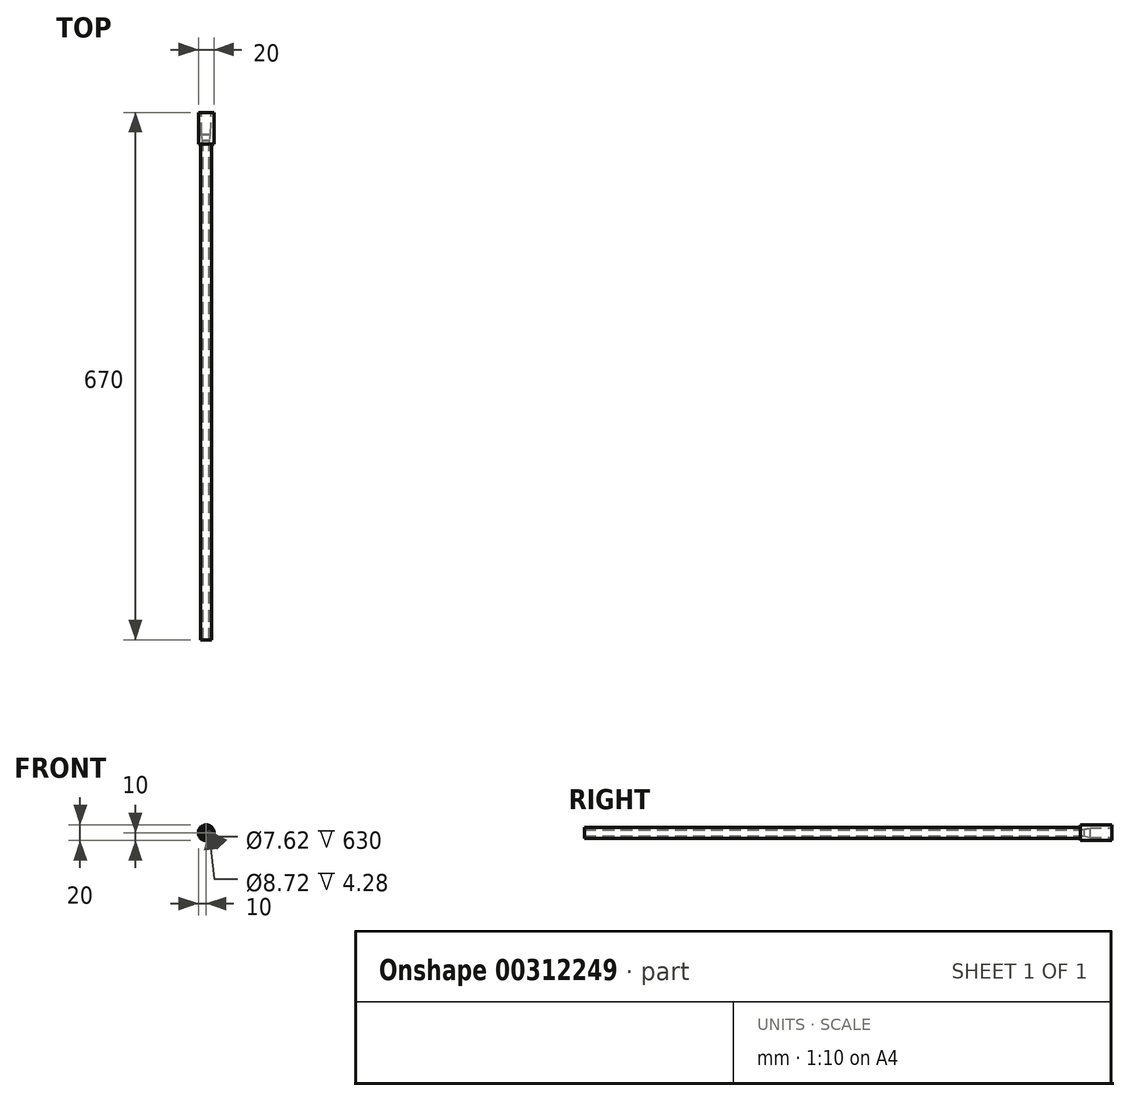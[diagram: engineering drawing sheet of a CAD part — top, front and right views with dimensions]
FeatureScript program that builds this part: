
annotation { "Feature Type Name" : "Feature", "Feature Type Description" : "" }
export const myFeature = defineFeature(function(context is Context, id is Id, definition is map)
    precondition{}
    {
        {
            var Q0;
            Q0=qCreatedBy(makeId("Front.planeOp"),FACE);
            var sketch = newSketch(context, id + "F0", { "sketchPlane" : qUnion([Q0])});
            skCircle(sketch, "E0", {"center": v(0, 0) * mm, "radius": 7 * mm});
            skCircle(sketch, "E1", {"center": v(0, 0) * mm, "radius": 3.81 * mm});
            skSolve(sketch);
        }
        {
            var Q0;
            Q0=makeQuery(id+"F0.imprint","IMPRINT",FACE,{"disambiguationData":[TD([[makeQuery(id+"F0.imprint","IMPRINT",EDGE,{"derivedFrom":sQuery(id+"F0.wireOp",EDGE,"E0")}),1.0]])]});
            extrude(context, id + "F1", {"entities" : qUnion([Q0]), "depth" : 630 * mm});
        }
        {
            var Q0;
            Q0=makeQuery(id+"F1.opExtrude","CAP_FACE",FACE,{"disambiguationData":[OSD([sQuery(id+"F0.wireOp",EDGE,"E0"),sQuery(id+"F0.wireOp",EDGE,"E1")])],"isStart":true});
            var sketch = newSketch(context, id + "F2", { "sketchPlane" : qUnion([Q0])});
            skCircle(sketch, "E2", {"center": v(0, 0) * mm, "radius": 10 * mm});
            skSolve(sketch);
        }
        {
            var Q0;
            Q0=makeQuery(id+"F2.imprint","IMPRINT",FACE,{"disambiguationData":[TD([[makeQuery(id+"F2.imprint","IMPRINT",EDGE,{"derivedFrom":sQuery(id+"F2.wireOp",EDGE,"E2")}),1.0]])]});
            var Q1;
            Q1=makeQuery(id+"F2.imprint","IMPRINT",FACE,{"disambiguationData":[TD([[makeQuery(id+"F2.imprint","IMPRINT",EDGE,{"derivedFrom":makeQuery(id+"F1.opExtrude","CAP_EDGE",EDGE,{"disambiguationData":[OSD([sQuery(id+"F0.wireOp",EDGE,"E0")])],"isStart":true})}),-1.0]])]});
            extrude(context, id + "F3", {"entities" : qUnion([Q0, Q1]), "operationType" : NewBodyOperationType.ADD, "depth" : 40 * mm});
        }
        {
            var Q0;
            Q0=qCreatedBy(makeId("Right.planeOp"),FACE);
            var sketch = newSketch(context, id + "F4", { "sketchPlane" : qUnion([Q0])});
            skLineSegment(sketch, "E3.bottom", {"start": v(0, 0) * mm, "end": v(4.28, 0) * mm});
            skLineSegment(sketch, "E3.top", {"start": v(0, 4.36) * mm, "end": v(4.28, 4.36) * mm});
            skLineSegment(sketch, "E3.left", {"start": v(0, 0) * mm, "end": v(0, 4.36) * mm});
            skLineSegment(sketch, "E3.right", {"start": v(4.28, 0) * mm, "end": v(4.28, 4.36) * mm});
            skLineSegment(sketch, "E4", {"start": v(11.98, 0) * mm, "end": v(11.98, 5.77) * mm});
            skLineSegment(sketch, "E5", {"start": v(4.28, 4.36) * mm, "end": v(11.98, 5.77) * mm});
            skLineSegment(sketch, "E6", {"start": v(4.28, 0) * mm, "end": v(11.98, 0) * mm});
            skLineSegment(sketch, "E7", {"start": v(11.98, 0) * mm, "end": v(47.75, 0) * mm});
            skLineSegment(sketch, "E8", {"start": v(47.75, 0) * mm, "end": v(47.75, 5.98) * mm});
            skLineSegment(sketch, "E9", {"start": v(11.98, 5.76) * mm, "end": v(47.75, 5.98) * mm});
            skSolve(sketch);
        }
        {
            var Q0;
            Q0 = qSketchRegion(id + "F4", true);
            var Q1;
            Q1=sQuery(id+"F4.wireOp",EDGE,"E7");
            revolve(context, id + "F5", {"operationType" : NewBodyOperationType.REMOVE, "entities" : qUnion([Q0]), "axis" : qUnion([Q1]), "revolveType" : RevolveType.FULL, "oppositeDirection" : true});
        }
    });
